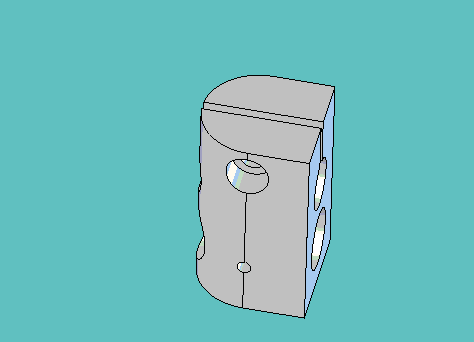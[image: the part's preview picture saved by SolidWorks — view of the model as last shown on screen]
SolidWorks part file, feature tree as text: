
SOLIDWORKS PART (.sldprt)
format: sldprt  version: not decoded by parser v0  size: 303,616 bytes
history: native  units: mm
features: sketch x10, extrude x8, revolve x2, material x1, plane x1, boolean_combine x1 (+11 scaffold rows collapsed)
feature tree (34):
  scaffold x11  (default folders/planes/origin — collapsed)
  material  "Material <not specified>"
  sketch  "Sketch1"  dims[D1=33.3375mm D2=9.525mm D3=153.9875mm]
  revolve  "Revolve1"  Angle=360deg
  sketch  "Sketch14"  dims[D1=10.16mm]
  extrude  "Extrude8"  [1 undecoded]
  sketch  "Sketch2"  dims[c1.D1=3.4544mm c1.D2=2.2606mm c1.D3=8.7376mm c1.D4=28.3464mm c2.D3=8.7376mm c2.D4=28.3464mm]
  extrude  "Extrude1"  [1 undecoded]
  sketch  "Sketch3"  dims[D1=2.2606mm]
  extrude  "Extrude2"  Depth=7.9756mm
  sketch  "Sketch5"  dims[c1.D4=~4.437453mm c1.D5=6.35mm c1.D1=8.7376mm c1.D2=6.35mm c1.D3=6.35mm c2.D4=9.525mm c2.D2=9.525mm c3.D4=9.525mm c3.D6=12.7mm c4.D4=6.35mm]
  revolve  "Revolve2"  Angle=360deg
  sketch  "Sketch11"  dims[D1=~10.31875mm]
  sketch  "Sketch6"  dims[D1=~8.73125mm D2=20.6502mm]
  extrude  "Extrude3"  [1 undecoded]
  sketch  "Sketch9"  dims[c1.D1=4.3688mm c1.D2=2.2606mm c1.D3=8.7376mm c1.D4=28.3464mm c2.D3=8.7376mm c2.D4=28.3464mm]
  extrude  "Extrude5"  [1 undecoded]
  plane  "Plane1"  Offset=12.7mm
  sketch  "Sketch10"  dims[D1=~7.14375mm]
  extrude  "Extrude6"  Depth=7.9375mm
  sketch  "Sketch13"  dims[D1=~0.79375mm D2=~0.79375mm]
  extrude  "Extrude7"  Depth=12.7mm
  extrude  "Extrude9"  [1 undecoded]
  boolean_combine  "Combine1"
decode coverage: 15 of 21 modeling features carry decoded parameters
note: ~ marks probable driven/reference dimensions
note: 5 parameter values undecoded
summary: no parameter record found for 5 features
note: suppression state not decoded; provenance and decode notes live in map.json
